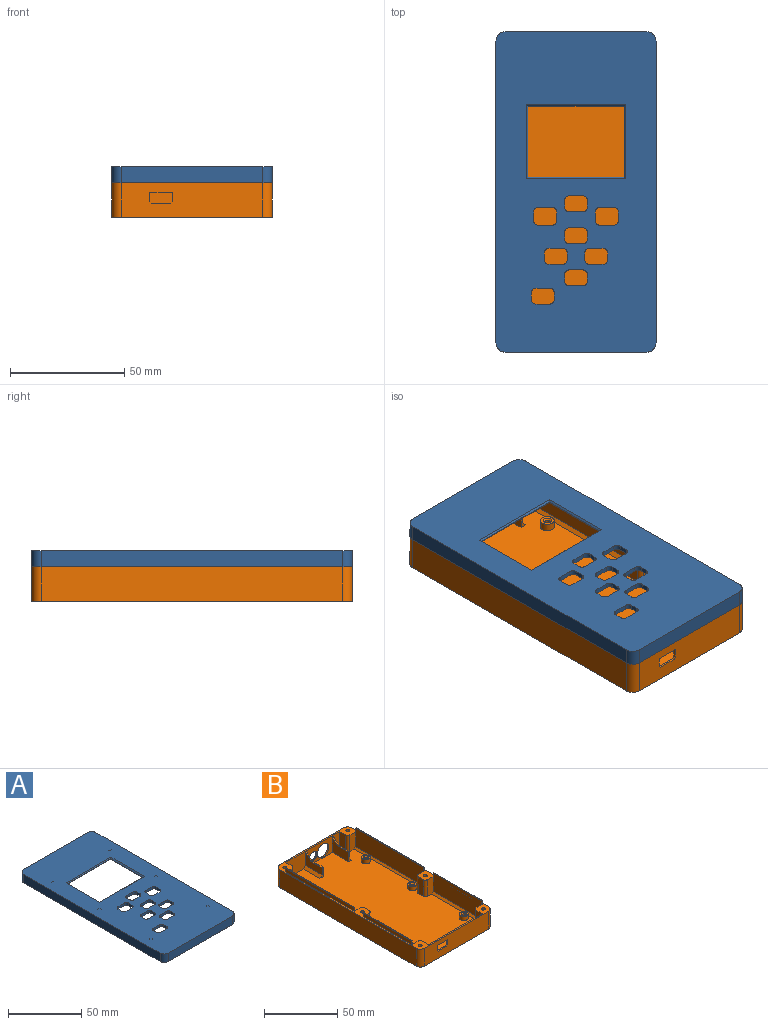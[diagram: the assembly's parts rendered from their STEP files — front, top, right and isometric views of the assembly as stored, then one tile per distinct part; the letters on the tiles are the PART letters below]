
ASSEMBLY  parts=2 mates=1
PART A: 177 faces, bbox 70x140x8 mm
  f0: plane 133x64mm, normal (0,0,-1), area 4401.4mm2, adj f1,f2,f3,f4,f20,f21,f22,f23
  f1: plane 6x5.5mm, normal (-1,0,0), area 31mm2, adj f0,f7,f37,f169,f174
  f2: plane 6x5.5mm, normal (1,0,0), area 31mm2, adj f0,f7,f33,f169,f174
  f3: plane 6x5.5mm, normal (-1,0,0), area 31mm2, adj f0,f7,f36,f164,f171
  f4: plane 6x5.5mm, normal (1,0,0), area 31mm2, adj f0,f7,f32,f164,f171
  f5: plane 140x70mm, normal (0,0,1), area 7832mm2, adj f12,f13,f14,f15,f16,f17,f18,f19
  f6: plane 55x44mm, normal (0,0,-1), area 1871.8mm2, adj f85,f86,f87,f88,f89,f90,f91,f92
  f7: plane 140x70mm, normal (0,0,-1), area 737.5mm2, adj f1,f2,f3,f4,f8,f9,f10,f11
  f8: plane 47x4mm, normal (1,0,0), area 188mm2, adj f7,f26,f27,f173
  f9: plane 66x4mm, normal (1,0,0), area 264mm2, adj f7,f25,f28,f175
  f10: plane 66x4mm, normal (-1,0,0), area 264mm2, adj f7,f20,f24,f176
  f11: plane 47x4mm, normal (-1,0,0), area 188mm2, adj f7,f21,f23,f172
  f12: plane 62x7mm, normal (0,-1,0), area 434mm2, adj f5,f7,f16,f19
  f13: plane 132x7mm, normal (1,0,0), area 924mm2, adj f5,f7,f16,f17
  f14: plane 62x7mm, normal (0,1,0), area 434mm2, adj f5,f7,f17,f18
  f15: plane 132x7mm, normal (-1,0,0), area 924mm2, adj f5,f7,f18,f19
  f16: cylinder r=4mm len=7mm, axis (0,0,1), area 44mm2, adj f5,f7,f12,f13
  f17: cylinder r=4mm len=7mm, axis (0,0,-1), area 44mm2, adj f5,f7,f13,f14
  f18: cylinder r=4mm len=7mm, axis (0,0,1), area 44mm2, adj f5,f7,f14,f15
  f19: cylinder r=4mm len=7mm, axis (0,0,-1), area 44mm2, adj f5,f7,f12,f15
  f20: plane 6x6mm, normal (0,-1,0), area 34mm2, adj f0,f7,f10,f37,f176
  f21: plane 6x6mm, normal (0,1,0), area 34mm2, adj f0,f7,f11,f36,f172
  f22: plane 6x5mm, normal (-1,0,0), area 30mm2, adj f0,f7,f34,f35
  f23: plane 6x6mm, normal (0,-1,0), area 34mm2, adj f0,f7,f11,f35,f172
  f24: plane 6x6mm, normal (0,1,0), area 34mm2, adj f0,f7,f10,f34,f176
  f25: plane 6x6mm, normal (0,-1,0), area 34mm2, adj f0,f7,f9,f33,f175
  f26: plane 6x6mm, normal (0,1,0), area 34mm2, adj f0,f7,f8,f32,f173
  f27: plane 6x6mm, normal (0,-1,0), area 34mm2, adj f0,f7,f8,f30,f173
  f28: plane 6x6mm, normal (0,1,0), area 34mm2, adj f0,f7,f9,f31,f175
  f29: plane 6x5mm, normal (1,0,0), area 30mm2, adj f0,f7,f30,f31
  f30: cylinder r=2mm len=6mm, axis (0,0,-1), area 18.8mm2, adj f0,f7,f27,f29
  f31: cylinder r=2mm len=6mm, axis (0,0,1), area 18.8mm2, adj f0,f7,f28,f29
  f32: cylinder r=2mm len=6mm, axis (0,0,1), area 18.8mm2, adj f0,f4,f7,f26
  f33: cylinder r=2mm len=6mm, axis (0,0,1), area 18.8mm2, adj f0,f2,f7,f25
  f34: cylinder r=2mm len=6mm, axis (0,0,1), area 18.8mm2, adj f0,f7,f22,f24
  f35: cylinder r=2mm len=6mm, axis (0,0,-1), area 18.8mm2, adj f0,f7,f22,f23
  f36: cylinder r=2mm len=6mm, axis (0,0,1), area 18.8mm2, adj f0,f3,f7,f21
  f37: cylinder r=2mm len=6mm, axis (0,0,1), area 18.8mm2, adj f0,f1,f7,f20
  f38: cylinder r=3.5mm len=7mm, axis (0,0,1), area 88mm2, adj f0,f39
  f39: plane 7x7mm, normal (0,0,-1), area 27.7mm2, adj f38,f62
  f40: cylinder r=2.5mm len=5mm, axis (0,0,1), area 62.8mm2, adj f0,f41
  f41: plane 5x5mm, normal (0,0,-1), area 8.9mm2, adj f40,f64
  f42: cylinder r=2.5mm len=5mm, axis (0,0,1), area 62.8mm2, adj f0,f43
  f43: plane 5x5mm, normal (0,0,-1), area 8.9mm2, adj f42,f67
  f44: cylinder r=2.5mm len=5mm, axis (0,0,1), area 62.8mm2, adj f0,f45
  f45: plane 5x5mm, normal (0,0,-1), area 8.9mm2, adj f44,f66
  f46: cylinder r=3.5mm len=7mm, axis (0,0,1), area 88mm2, adj f0,f47
  f47: plane 7x7mm, normal (0,0,-1), area 27.7mm2, adj f46,f63
  f48: cylinder r=2.5mm len=5mm, axis (0,0,1), area 62.8mm2, adj f0,f49
  f49: plane 5x5mm, normal (0,0,-1), area 8.9mm2, adj f48,f65
  f50: cylinder r=1.15mm len=3.8mm, axis (0,0,-1), area 27.5mm2, adj f51,f65
  f51: plane 2.3x2.3mm, normal (0,0,-1), area 4.2mm2, adj f50
  f52: cylinder r=1.15mm len=3.8mm, axis (0,0,-1), area 27.5mm2, adj f53,f63
  f53: plane 2.3x2.3mm, normal (0,0,-1), area 4.2mm2, adj f52
  f54: cylinder r=1.15mm len=3.8mm, axis (0,0,-1), area 27.5mm2, adj f55,f66
  f55: plane 2.3x2.3mm, normal (0,0,-1), area 4.2mm2, adj f54
  f56: cylinder r=1.15mm len=3.8mm, axis (0,0,-1), area 27.5mm2, adj f57,f67
  f57: plane 2.3x2.3mm, normal (0,0,-1), area 4.2mm2, adj f56
  f58: cylinder r=1.15mm len=3.8mm, axis (0,0,-1), area 27.5mm2, adj f59,f64
  f59: plane 2.3x2.3mm, normal (0,0,-1), area 4.2mm2, adj f58
  f60: cylinder r=1.15mm len=3.8mm, axis (0,0,-1), area 27.5mm2, adj f61,f62
  f61: plane 2.3x2.3mm, normal (0,0,-1), area 4.2mm2, adj f60
  f62: cone r=1.15mm half-angle=45deg, axis (0,0,-1), area 9.3mm2, adj f39,f60
  f63: cone r=1.85mm half-angle=45deg, axis (0,0,-1), area 9.3mm2, adj f47,f52
  f64: cone r=1.15mm half-angle=45deg, axis (0,0,-1), area 9.3mm2, adj f41,f58
  f65: cone r=1.85mm half-angle=45deg, axis (0,0,-1), area 9.3mm2, adj f49,f50
  f66: cone r=1.85mm half-angle=45deg, axis (0,0,-1), area 9.3mm2, adj f45,f54
  f67: cone r=1.15mm half-angle=45deg, axis (0,0,-1), area 9.3mm2, adj f43,f56
  f68: cylinder r=1.15mm len=5.3mm, axis (0,0,-1), area 38.3mm2, adj f69,f84
  f69: plane 2.3x2.3mm, normal (0,0,-1), area 4.2mm2, adj f68
  f70: cylinder r=1.15mm len=6mm, axis (0,0,-1), area 43.4mm2, adj f7,f71
  f71: plane 2.3x2.3mm, normal (0,0,-1), area 4.2mm2, adj f70
  f72: cylinder r=1.15mm len=5.3mm, axis (0,0,-1), area 38.3mm2, adj f73,f80
  f73: plane 2.3x2.3mm, normal (0,0,-1), area 4.2mm2, adj f72
  f74: cylinder r=1.15mm len=5.3mm, axis (0,0,-1), area 38.3mm2, adj f75,f81
  f75: plane 2.3x2.3mm, normal (0,0,-1), area 4.2mm2, adj f74
  f76: cylinder r=1.15mm len=5.3mm, axis (0,0,-1), area 38.3mm2, adj f77,f82
  f77: plane 2.3x2.3mm, normal (0,0,-1), area 4.2mm2, adj f76
  f78: cylinder r=1.15mm len=5.3mm, axis (0,0,-1), area 38.3mm2, adj f79,f83
  f79: plane 2.3x2.3mm, normal (0,0,-1), area 4.2mm2, adj f78
  f80: cone r=1.15mm half-angle=45deg, axis (0,0,-1), area 9.3mm2, adj f7,f72
  f81: cone r=1.85mm half-angle=45deg, axis (0,0,-1), area 9.3mm2, adj f7,f74
  f82: cone r=1.85mm half-angle=45deg, axis (0,0,-1), area 9.3mm2, adj f7,f76
  f83: cone r=1.85mm half-angle=45deg, axis (0,0,-1), area 9.3mm2, adj f7,f78
  f84: cone r=1.15mm half-angle=45deg, axis (0,0,-1), area 9.3mm2, adj f7,f68
  f85: plane 44x1mm, normal (0,-1,0), area 44mm2, adj f0,f6,f86,f88
  f86: plane 55x1mm, normal (-1,0,0), area 55mm2, adj f0,f6,f85,f87
  f87: plane 44x1mm, normal (0,1,0), area 44mm2, adj f0,f6,f86,f88
  f88: plane 55x1mm, normal (1,0,0), area 55mm2, adj f0,f6,f85,f87
  f89: plane 6x2mm, normal (0,1,0), area 12mm2, adj f5,f6,f141,f144
  f90: plane 3.78x2mm, normal (-1,0,0), area 7.6mm2, adj f5,f6,f143,f144
  f91: plane 6x2mm, normal (0,-1,0), area 12mm2, adj f5,f6,f142,f143
  f92: plane 3.78x2mm, normal (1,0,0), area 7.6mm2, adj f5,f6,f141,f142
  f93: plane 6x2mm, normal (0,1,0), area 12mm2, adj f5,f6,f145,f148
  f94: plane 3x2mm, normal (-1,0,0), area 6mm2, adj f5,f6,f147,f148
  f95: plane 6x2mm, normal (0,-1,0), area 12mm2, adj f5,f6,f146,f147
  f96: plane 3x2mm, normal (1,0,0), area 6mm2, adj f5,f6,f145,f146
  f97: plane 6x2mm, normal (0,1,0), area 12mm2, adj f5,f6,f149,f152
  f98: plane 3x2mm, normal (-1,0,0), area 6mm2, adj f5,f6,f151,f152
  f99: plane 6x2mm, normal (0,-1,0), area 12mm2, adj f5,f6,f150,f151
  f100: plane 3x2mm, normal (1,0,0), area 6mm2, adj f5,f6,f149,f150
  f101: plane 6x2mm, normal (0,1,0), area 12mm2, adj f5,f6,f153,f156
  f102: plane 3x2mm, normal (-1,0,0), area 6mm2, adj f5,f6,f153,f154
  f103: plane 6x2mm, normal (0,-1,0), area 12mm2, adj f5,f6,f154,f155
  f104: plane 3x2mm, normal (1,0,0), area 6mm2, adj f5,f6,f155,f156
  f105: plane 6x2mm, normal (0,1,0), area 12mm2, adj f5,f6,f137,f140
  f106: plane 3x2mm, normal (-1,0,0), area 6mm2, adj f5,f6,f139,f140
  f107: plane 6x2mm, normal (0,-1,0), area 12mm2, adj f5,f6,f138,f139
  f108: plane 3x2mm, normal (1,0,0), area 6mm2, adj f5,f6,f137,f138
  f109: plane 6x2mm, normal (0,1,0), area 12mm2, adj f5,f6,f133,f136
  f110: plane 3x2mm, normal (-1,0,0), area 6mm2, adj f5,f6,f135,f136
  f111: plane 6x2mm, normal (0,-1,0), area 12mm2, adj f5,f6,f134,f135
  f112: plane 3x2mm, normal (1,0,0), area 6mm2, adj f5,f6,f133,f134
  f113: plane 3.78x2mm, normal (1,0,0), area 7.6mm2, adj f5,f6,f129,f132
  f114: plane 6x2mm, normal (0,1,0), area 12mm2, adj f5,f6,f131,f132
  f115: plane 3.78x2mm, normal (-1,0,0), area 7.6mm2, adj f5,f6,f130,f131
  f116: plane 6x2mm, normal (0,-1,0), area 12mm2, adj f5,f6,f129,f130
  f117: plane 6x2mm, normal (0,-1,0), area 12mm2, adj f5,f6,f125,f128
  f118: plane 3x2mm, normal (1,0,0), area 6mm2, adj f5,f6,f127,f128
  f119: plane 6x2mm, normal (0,1,0), area 12mm2, adj f5,f6,f126,f127
  f120: plane 3x2mm, normal (-1,0,0), area 6mm2, adj f5,f6,f125,f126
  f121: plane 42x0.3mm, normal (0,1,0), area 12.6mm2, adj f0,f122,f124,f160
  f122: plane 31x0.3mm, normal (-1,0,0), area 9.3mm2, adj f0,f121,f123,f158
  f123: plane 42x0.3mm, normal (0,-1,0), area 12.6mm2, adj f0,f122,f124,f157
  f124: plane 31x0.3mm, normal (1,0,0), area 9.3mm2, adj f0,f121,f123,f159
  f125: cylinder r=2mm len=2mm, axis (0,0,1), area 6.3mm2, adj f5,f6,f117,f120
  f126: cylinder r=2mm len=2mm, axis (0,0,-1), area 6.3mm2, adj f5,f6,f119,f120
  f127: cylinder r=2mm len=2mm, axis (0,0,1), area 6.3mm2, adj f5,f6,f118,f119
  f128: cylinder r=2mm len=2mm, axis (0,0,-1), area 6.3mm2, adj f5,f6,f117,f118
  f129: cylinder r=2mm len=2mm, axis (0,0,-1), area 6.3mm2, adj f5,f6,f113,f116
  f130: cylinder r=2mm len=2mm, axis (0,0,1), area 6.3mm2, adj f5,f6,f115,f116
  f131: cylinder r=2mm len=2mm, axis (0,0,-1), area 6.3mm2, adj f5,f6,f114,f115
  f132: cylinder r=2mm len=2mm, axis (0,0,1), area 6.3mm2, adj f5,f6,f113,f114
  f133: cylinder r=2mm len=2mm, axis (0,0,-1), area 6.3mm2, adj f5,f6,f109,f112
  f134: cylinder r=2mm len=2mm, axis (0,0,1), area 6.3mm2, adj f5,f6,f111,f112
  f135: cylinder r=2mm len=2mm, axis (0,0,-1), area 6.3mm2, adj f5,f6,f110,f111
  f136: cylinder r=2mm len=2mm, axis (0,0,1), area 6.3mm2, adj f5,f6,f109,f110
  f137: cylinder r=2mm len=2mm, axis (0,0,-1), area 6.3mm2, adj f5,f6,f105,f108
  f138: cylinder r=2mm len=2mm, axis (0,0,1), area 6.3mm2, adj f5,f6,f107,f108
  f139: cylinder r=2mm len=2mm, axis (0,0,-1), area 6.3mm2, adj f5,f6,f106,f107
  f140: cylinder r=2mm len=2mm, axis (0,0,1), area 6.3mm2, adj f5,f6,f105,f106
  f141: cylinder r=2mm len=2mm, axis (0,0,-1), area 6.3mm2, adj f5,f6,f89,f92
  f142: cylinder r=2mm len=2mm, axis (0,0,1), area 6.3mm2, adj f5,f6,f91,f92
  f143: cylinder r=2mm len=2mm, axis (0,0,-1), area 6.3mm2, adj f5,f6,f90,f91
  f144: cylinder r=2mm len=2mm, axis (0,0,1), area 6.3mm2, adj f5,f6,f89,f90
  f145: cylinder r=2mm len=2mm, axis (0,0,-1), area 6.3mm2, adj f5,f6,f93,f96
  f146: cylinder r=2mm len=2mm, axis (0,0,1), area 6.3mm2, adj f5,f6,f95,f96
  f147: cylinder r=2mm len=2mm, axis (0,0,-1), area 6.3mm2, adj f5,f6,f94,f95
  f148: cylinder r=2mm len=2mm, axis (0,0,1), area 6.3mm2, adj f5,f6,f93,f94
  f149: cylinder r=2mm len=2mm, axis (0,0,-1), area 6.3mm2, adj f5,f6,f97,f100
  f150: cylinder r=2mm len=2mm, axis (0,0,1), area 6.3mm2, adj f5,f6,f99,f100
  f151: cylinder r=2mm len=2mm, axis (0,0,-1), area 6.3mm2, adj f5,f6,f98,f99
  f152: cylinder r=2mm len=2mm, axis (0,0,1), area 6.3mm2, adj f5,f6,f97,f98
  f153: cylinder r=2mm len=2mm, axis (0,0,1), area 6.3mm2, adj f5,f6,f101,f102
  f154: cylinder r=2mm len=2mm, axis (0,0,-1), area 6.3mm2, adj f5,f6,f102,f103
  f155: cylinder r=2mm len=2mm, axis (0,0,1), area 6.3mm2, adj f5,f6,f103,f104
  f156: cylinder r=2mm len=2mm, axis (0,0,-1), area 6.3mm2, adj f5,f6,f101,f104
  f157: plane 43.4x0.7mm, normal (0,-0.71,0.71), area 42.3mm2, adj f5,f123,f158,f159
  f158: plane 32.4x0.7mm, normal (-0.71,0,0.71), area 31.4mm2, adj f5,f122,f157,f160
  f159: plane 32.4x0.7mm, normal (0.71,0,0.71), area 31.4mm2, adj f5,f124,f157,f160
  f160: plane 43.4x0.7mm, normal (0,0.71,0.71), area 42.3mm2, adj f5,f121,f158,f159
  f161: plane 1x0.5mm, normal (1,0,0), area 0.5mm2, adj f7,f162,f164,f165
  f162: plane 52x1mm, normal (0,-1,0), area 52mm2, adj f7,f161,f163,f165
  f163: plane 1x0.5mm, normal (-1,0,0), area 0.5mm2, adj f7,f162,f164,f165
  f164: plane 52x5mm, normal (0,1,0), area 260mm2, adj f3,f4,f161,f163,f165,f171
  f165: plane 52x0.5mm, normal (0,0,-1), area 26mm2, adj f161,f162,f163,f164
  f166: plane 1x0.5mm, normal (1,0,0), area 0.5mm2, adj f7,f168,f169,f170
  f167: plane 1x0.5mm, normal (-1,0,0), area 0.5mm2, adj f7,f168,f169,f170
  f168: plane 52x1mm, normal (0,1,0), area 52mm2, adj f7,f166,f167,f170
  f169: plane 52x5mm, normal (0,-1,0), area 260mm2, adj f1,f2,f166,f167,f170,f174
  f170: plane 52x0.5mm, normal (0,0,-1), area 26mm2, adj f166,f167,f168,f169
  f171: plane 52x2mm, normal (0,0.71,-0.71), area 147.1mm2, adj f0,f3,f4,f164
  f172: plane 47x2mm, normal (-0.71,0,-0.71), area 132.9mm2, adj f0,f11,f21,f23
  f173: plane 47x2mm, normal (0.71,0,-0.71), area 132.9mm2, adj f0,f8,f26,f27
  f174: plane 52x2mm, normal (0,-0.71,-0.71), area 147.1mm2, adj f0,f1,f2,f169
  f175: plane 66x2mm, normal (0.71,0,-0.71), area 186.7mm2, adj f0,f9,f25,f28
  f176: plane 66x2mm, normal (-0.71,0,-0.71), area 186.7mm2, adj f0,f10,f20,f24
PART B: 121 faces, bbox 70x140x18 mm
  f0: plane 52x14mm, normal (0,1,0), area 678.6mm2, adj f4,f6,f28,f37,f109,f110,f111,f112
  f1: plane 62x15mm, normal (0,-1,0), area 880.6mm2, adj f4,f5,f11,f14,f109,f110,f111,f112
  f2: plane 47x1.5mm, normal (-0.71,0,0.71), area 99.7mm2, adj f6,f36,f39,f104
  f3: plane 66x1.5mm, normal (-0.71,0,0.71), area 140mm2, adj f6,f35,f38,f99
  f4: plane 140x70mm, normal (0,0,1), area 763.5mm2, adj f0,f1,f7,f8,f9,f10,f11,f12
  f5: plane 140x70mm, normal (0,0,-1), area 9616.6mm2, adj f1,f8,f9,f10,f11,f12,f13,f14
  f6: plane 138x64mm, normal (0,0,1), area 8273.2mm2, adj f0,f2,f3,f7,f15,f17,f19,f21
  f7: plane 52x14mm, normal (0,-1,0), area 564.5mm2, adj f4,f6,f30,f34,f61,f63,f65,f67
  f8: plane 132x15mm, normal (1,0,0), area 1980mm2, adj f4,f5,f11,f12
  f9: plane 62x15mm, normal (0,1,0), area 796.5mm2, adj f4,f5,f12,f13,f71,f72
  f10: plane 132x15mm, normal (-1,0,0), area 1980mm2, adj f4,f5,f13,f14
  f11: cylinder r=4mm len=15mm, axis (0,0,1), area 94.2mm2, adj f1,f4,f5,f8
  f12: cylinder r=4mm len=15mm, axis (0,0,-1), area 94.2mm2, adj f4,f5,f8,f9
  f13: cylinder r=4mm len=15mm, axis (0,0,1), area 94.2mm2, adj f4,f5,f9,f10
  f14: cylinder r=4mm len=15mm, axis (0,0,-1), area 94.2mm2, adj f1,f4,f5,f10
  f15: cylinder r=3mm len=6mm, axis (0,0,-1), area 64.1mm2, adj f6,f16
  f16: plane 6x6mm, normal (0,0,1), area 17.5mm2, adj f15,f118
  f17: cylinder r=3mm len=6mm, axis (0,0,-1), area 64.1mm2, adj f6,f18
  f18: plane 6x6mm, normal (0,0,1), area 17.5mm2, adj f17,f119
  f19: cylinder r=3mm len=6mm, axis (0,0,-1), area 64.1mm2, adj f6,f20
  f20: plane 6x6mm, normal (0,0,1), area 17.5mm2, adj f19,f120
  f21: cylinder r=3mm len=6mm, axis (0,0,-1), area 64.1mm2, adj f6,f22
  f22: plane 6x6mm, normal (0,0,1), area 17.5mm2, adj f21,f117
  f23: cylinder r=3mm len=6mm, axis (0,0,-1), area 64.1mm2, adj f6,f24
  f24: plane 6x6mm, normal (0,0,1), area 17.5mm2, adj f23,f115
  f25: cylinder r=3mm len=6mm, axis (0,0,-1), area 64.1mm2, adj f6,f26
  f26: plane 6x6mm, normal (0,0,1), area 17.5mm2, adj f25,f116
  f27: plane 14x5.5mm, normal (0,1,0), area 75.9mm2, adj f4,f6,f60,f82,f94
  f28: plane 14x6mm, normal (1,0,0), area 84mm2, adj f0,f4,f6,f60
  f29: plane 14x5.5mm, normal (0,-1,0), area 75.9mm2, adj f4,f6,f59,f81,f89
  f30: plane 14x6mm, normal (1,0,0), area 84mm2, adj f4,f6,f7,f59
  f31: plane 14x5.5mm, normal (0,1,0), area 75.9mm2, adj f4,f6,f58,f81,f89
  f32: plane 14x5.5mm, normal (0,-1,0), area 75.9mm2, adj f4,f6,f57,f82,f94
  f33: plane 14x5mm, normal (1,0,0), area 70mm2, adj f4,f6,f57,f58
  f34: plane 14x6mm, normal (-1,0,0), area 84mm2, adj f4,f6,f7,f56
  f35: plane 14x5.5mm, normal (0,-1,0), area 75.9mm2, adj f3,f4,f6,f56,f99
  f36: plane 14x5.5mm, normal (0,1,0), area 75.9mm2, adj f2,f4,f6,f55,f104
  f37: plane 14x6mm, normal (-1,0,0), area 84mm2, adj f0,f4,f6,f55
  f38: plane 14x5.5mm, normal (0,1,0), area 75.9mm2, adj f3,f4,f6,f53,f99
  f39: plane 14x5.5mm, normal (0,-1,0), area 75.9mm2, adj f2,f4,f6,f54,f104
  f40: plane 14x5mm, normal (-1,0,0), area 70mm2, adj f4,f6,f53,f54
  f41: cylinder r=1.15mm len=3.3mm, axis (0,0,1), area 23.8mm2, adj f42,f116
  f42: plane 2.3x2.3mm, normal (0,0,1), area 4.2mm2, adj f41
  f43: cylinder r=1.15mm len=3.3mm, axis (0,0,1), area 23.8mm2, adj f44,f115
  f44: plane 2.3x2.3mm, normal (0,0,1), area 4.2mm2, adj f43
  f45: cylinder r=1.15mm len=3.3mm, axis (0,0,1), area 23.8mm2, adj f46,f117
  f46: plane 2.3x2.3mm, normal (0,0,1), area 4.2mm2, adj f45
  f47: cylinder r=1.15mm len=3.3mm, axis (0,0,1), area 23.8mm2, adj f48,f120
  f48: plane 2.3x2.3mm, normal (0,0,1), area 4.2mm2, adj f47
  f49: cylinder r=1.15mm len=3.3mm, axis (0,0,1), area 23.8mm2, adj f50,f119
  f50: plane 2.3x2.3mm, normal (0,0,1), area 4.2mm2, adj f49
  f51: cylinder r=1.15mm len=3.3mm, axis (0,0,1), area 23.8mm2, adj f52,f118
  f52: plane 2.3x2.3mm, normal (0,0,1), area 4.2mm2, adj f51
  f53: cylinder r=2mm len=14mm, axis (0,0,-1), area 44mm2, adj f4,f6,f38,f40
  f54: cylinder r=2mm len=14mm, axis (0,0,1), area 44mm2, adj f4,f6,f39,f40
  f55: cylinder r=2mm len=14mm, axis (0,0,1), area 44mm2, adj f4,f6,f36,f37
  f56: cylinder r=2mm len=14mm, axis (0,0,1), area 44mm2, adj f4,f6,f34,f35
  f57: cylinder r=2mm len=14mm, axis (0,0,1), area 44mm2, adj f4,f6,f32,f33
  f58: cylinder r=2mm len=14mm, axis (0,0,-1), area 44mm2, adj f4,f6,f31,f33
  f59: cylinder r=2mm len=14mm, axis (0,0,1), area 44mm2, adj f4,f6,f29,f30
  f60: cylinder r=2mm len=14mm, axis (0,0,1), area 44mm2, adj f4,f6,f27,f28
  f61: plane 16x11mm, normal (-1,0,0), area 108.5mm2, adj f7,f62,f64,f70,f80
  f62: plane 8x3mm, normal (0,-1,0), area 10mm2, adj f6,f61,f63,f64,f80
  f63: plane 16x13mm, normal (1,0,0), area 140.5mm2, adj f6,f7,f62,f64,f70
  f64: plane 11x1mm, normal (0,0,1), area 11mm2, adj f61,f62,f63,f70
  f65: plane 16x13mm, normal (-1,0,0), area 140.5mm2, adj f6,f7,f66,f68,f69
  f66: plane 8x3mm, normal (0,-1,0), area 10mm2, adj f6,f65,f67,f68,f79
  f67: plane 16x11mm, normal (1,0,0), area 108.5mm2, adj f7,f66,f68,f69,f79
  f68: plane 11x1mm, normal (0,0,1), area 11mm2, adj f65,f66,f67,f69
  f69: plane 5x5mm, normal (0,-0.71,0.71), area 7.1mm2, adj f7,f65,f67,f68
  f70: plane 5x5mm, normal (0,-0.71,0.71), area 7.1mm2, adj f7,f61,f63,f64
  f71: cylinder r=5.5mm len=11mm, axis (0,-1,0), area 34.6mm2, adj f7,f9
  f72: cylinder r=3.5mm len=7mm, axis (0,-1,0), area 22mm2, adj f7,f9
  f73: cylinder r=1.3mm len=13.3mm, axis (0,0,1), area 108.6mm2, adj f4,f83
  f74: cylinder r=1.3mm len=13.3mm, axis (0,0,1), area 108.6mm2, adj f4,f86
  f75: cylinder r=1.3mm len=13.3mm, axis (0,0,1), area 108.6mm2, adj f4,f88
  f76: cylinder r=1.3mm len=13.3mm, axis (0,0,1), area 108.6mm2, adj f4,f87
  f77: cylinder r=1.3mm len=13.3mm, axis (0,0,1), area 108.6mm2, adj f4,f85
  f78: cylinder r=1.3mm len=13.3mm, axis (0,0,1), area 108.6mm2, adj f4,f84
  f79: plane 16x2mm, normal (0.71,0,0.71), area 45.3mm2, adj f6,f7,f66,f67
  f80: plane 16x2mm, normal (-0.71,0,0.71), area 45.3mm2, adj f6,f7,f61,f62
  f81: plane 66x1.5mm, normal (0.71,0,0.71), area 140mm2, adj f6,f29,f31,f89
  f82: plane 47x1.5mm, normal (0.71,0,0.71), area 99.7mm2, adj f6,f27,f32,f94
  f83: cone r=3mm half-angle=45deg, axis (0,0,-1), area 32.5mm2, adj f5,f73
  f84: cone r=1.3mm half-angle=45deg, axis (0,0,-1), area 32.5mm2, adj f5,f78
  f85: cone r=1.3mm half-angle=45deg, axis (0,0,-1), area 32.5mm2, adj f5,f77
  f86: cone r=3mm half-angle=45deg, axis (0,0,-1), area 32.5mm2, adj f5,f74
  f87: cone r=1.3mm half-angle=45deg, axis (0,0,-1), area 32.5mm2, adj f5,f76
  f88: cone r=3mm half-angle=45deg, axis (0,0,-1), area 32.5mm2, adj f5,f75
  f89: plane 66x15.5mm, normal (1,0,0), area 1023mm2, adj f29,f31,f81,f90,f92,f93
  f90: plane 3x0.5mm, normal (0,1,0), area 1.5mm2, adj f4,f89,f91,f93
  f91: plane 66x3mm, normal (-1,0,0), area 198mm2, adj f4,f90,f92,f93
  f92: plane 3x0.5mm, normal (0,-1,0), area 1.5mm2, adj f4,f89,f91,f93
  f93: plane 66x0.5mm, normal (0,0,1), area 33mm2, adj f89,f90,f91,f92
  f94: plane 47x15.5mm, normal (1,0,0), area 728.5mm2, adj f27,f32,f82,f95,f97,f98
  f95: plane 3x0.5mm, normal (0,1,0), area 1.5mm2, adj f4,f94,f96,f98
  f96: plane 47x3mm, normal (-1,0,0), area 141mm2, adj f4,f95,f97,f98
  f97: plane 3x0.5mm, normal (0,-1,0), area 1.5mm2, adj f4,f94,f96,f98
  f98: plane 47x0.5mm, normal (0,0,1), area 23.5mm2, adj f94,f95,f96,f97
  f99: plane 66x15.5mm, normal (-1,0,0), area 1023mm2, adj f3,f35,f38,f100,f101,f103
  f100: plane 3x0.5mm, normal (0,1,0), area 1.5mm2, adj f4,f99,f102,f103
  f101: plane 3x0.5mm, normal (0,-1,0), area 1.5mm2, adj f4,f99,f102,f103
  f102: plane 66x3mm, normal (1,0,0), area 198mm2, adj f4,f100,f101,f103
  f103: plane 66x0.5mm, normal (0,0,1), area 33mm2, adj f99,f100,f101,f102
  f104: plane 47x15.5mm, normal (-1,0,0), area 728.5mm2, adj f2,f36,f39,f105,f106,f108
  f105: plane 3x0.5mm, normal (0,1,0), area 1.5mm2, adj f4,f104,f107,f108
  f106: plane 3x0.5mm, normal (0,-1,0), area 1.5mm2, adj f4,f104,f107,f108
  f107: plane 47x3mm, normal (1,0,0), area 141mm2, adj f4,f105,f106,f108
  f108: plane 47x0.5mm, normal (0,0,1), area 23.5mm2, adj f104,f105,f106,f107
  f109: plane 10x1mm, normal (0,0,-1), area 10mm2, adj f0,f1,f110,f112
  f110: plane 4.2x1mm, normal (1,0,0), area 4.2mm2, adj f0,f1,f109,f114
  f111: plane 8.4x1mm, normal (0,0,1), area 8.4mm2, adj f0,f1,f113,f114
  f112: plane 4.2x1mm, normal (-1,0,0), area 4.2mm2, adj f0,f1,f109,f113
  f113: plane 1x0.8mm, normal (-0.71,0,0.71), area 1.1mm2, adj f0,f1,f111,f112
  f114: plane 1x0.8mm, normal (0.71,0,0.71), area 1.1mm2, adj f0,f1,f110,f111
  f115: cone r=1.15mm half-angle=45deg, axis (0,0,1), area 9.3mm2, adj f24,f43
  f116: cone r=1.15mm half-angle=45deg, axis (0,0,1), area 9.3mm2, adj f26,f41
  f117: cone r=1.15mm half-angle=45deg, axis (0,0,1), area 9.3mm2, adj f22,f45
  f118: cone r=1.85mm half-angle=45deg, axis (0,0,1), area 9.3mm2, adj f16,f51
  f119: cone r=1.85mm half-angle=45deg, axis (0,0,1), area 9.3mm2, adj f18,f49
  f120: cone r=1.85mm half-angle=45deg, axis (0,0,1), area 9.3mm2, adj f20,f47
PLACE A t=(-23.98,-7.66,-29.72)mm
PLACE B t=(-23.98,-7.66,0.28)mm
MATE fastened A.f68 <-> B.f75  axis (0,0,-1) through (-54.48,-73.16,15.28)mm
